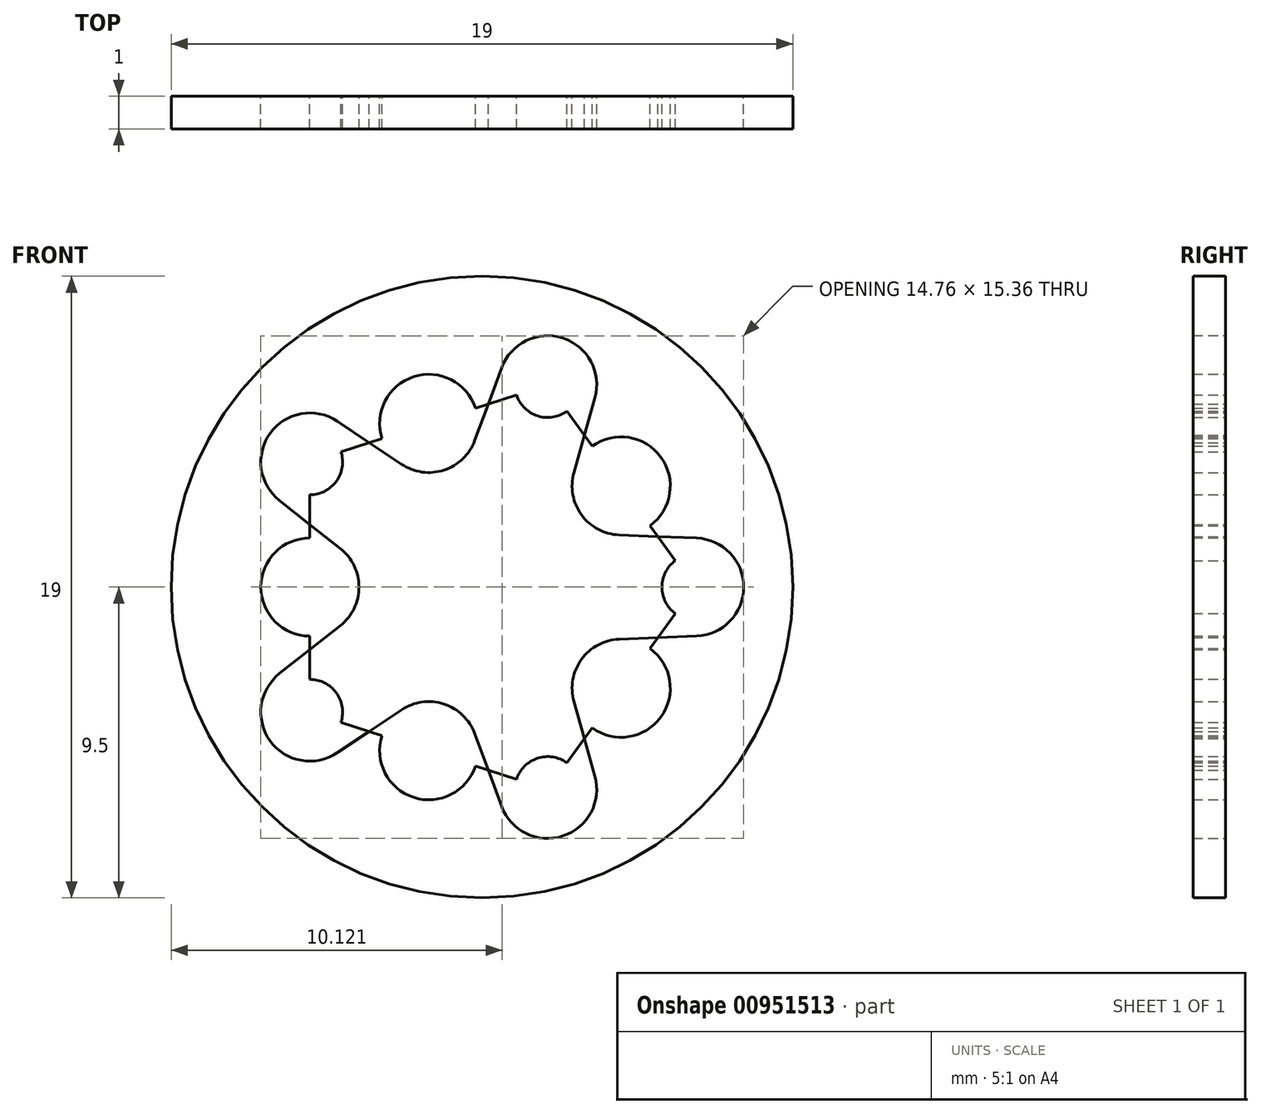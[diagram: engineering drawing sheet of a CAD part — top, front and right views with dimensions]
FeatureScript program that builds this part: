
annotation { "Feature Type Name" : "Feature", "Feature Type Description" : "" }
export const myFeature = defineFeature(function(context is Context, id is Id, definition is map)
    precondition{}
    {
        {
            var Q0;
            Q0=qCreatedBy(makeId("Front.planeOp"),FACE);
            var sketch = newSketch(context, id + "F0", { "sketchPlane" : qUnion([Q0])});
            skCircle(sketch, "E0", {"center": v(0, 0) * mm, "radius": 2.5 * mm});
            skCircle(sketch, "E1.cCircle", {"center": v(0, 0) * mm, "radius": 5.26 * mm, "construction": true});
            skLineSegment(sketch, "E1.0", {"start": v(-5.26, -3.82) * mm, "end": v(-5.26, 3.82) * mm});
            skLineSegment(sketch, "E1.1", {"start": v(-5.26, 3.82) * mm, "end": v(2, 6.18) * mm});
            skLineSegment(sketch, "E1.2", {"start": v(2, 6.18) * mm, "end": v(6.5, 0) * mm});
            skLineSegment(sketch, "E1.3", {"start": v(6.5, 0) * mm, "end": v(2, -6.18) * mm});
            skLineSegment(sketch, "E1.4", {"start": v(2, -6.18) * mm, "end": v(-5.26, -3.82) * mm});
            skPoint(sketch, "E1.0.midPoint", {"position": v(-5.26, 0) * mm});
            skCircle(sketch, "E2", {"center": v(-5.26, 3.82) * mm, "radius": 1 * mm});
            skCircle(sketch, "E3", {"center": v(2, 6.18) * mm, "radius": 1 * mm});
            skCircle(sketch, "E4", {"center": v(6.5, 0) * mm, "radius": 1 * mm});
            skCircle(sketch, "E5", {"center": v(2, -6.18) * mm, "radius": 1 * mm});
            skCircle(sketch, "E6", {"center": v(-5.26, -3.82) * mm, "radius": 1 * mm});
            skCircle(sketch, "E7", {"center": v(-5.26, 3.82) * mm, "radius": 1.5 * mm});
            skCircle(sketch, "E8", {"center": v(2, 6.18) * mm, "radius": 1.5 * mm});
            skCircle(sketch, "E9", {"center": v(6.5, 0) * mm, "radius": 1.5 * mm});
            skCircle(sketch, "E10", {"center": v(2, -6.18) * mm, "radius": 1.5 * mm});
            skCircle(sketch, "E11", {"center": v(-5.26, -3.82) * mm, "radius": 1.5 * mm});
            skCircle(sketch, "E12", {"center": v(-5.26, 0) * mm, "radius": 1.5 * mm});
            skCircle(sketch, "E13", {"center": v(-1.62, 5) * mm, "radius": 1.5 * mm});
            skCircle(sketch, "E14", {"center": v(4.25, 3.1) * mm, "radius": 1.5 * mm});
            skCircle(sketch, "E15", {"center": v(4.25, -3.1) * mm, "radius": 1.5 * mm});
            skCircle(sketch, "E16", {"center": v(-1.62, -5) * mm, "radius": 1.5 * mm});
            skLineSegment(sketch, "E17", {"start": v(-6.19, 2.64) * mm, "end": v(-4.33, 1.18) * mm});
            skLineSegment(sketch, "E18", {"start": v(-4.33, -1.18) * mm, "end": v(-6.19, -2.64) * mm});
            skLineSegment(sketch, "E19", {"start": v(-4.43, -5.07) * mm, "end": v(-2.46, -3.75) * mm});
            skLineSegment(sketch, "E20", {"start": v(-0.22, -4.48) * mm, "end": v(0.6, -6.7) * mm});
            skLineSegment(sketch, "E21", {"start": v(3.45, -5.77) * mm, "end": v(2.81, -3.5) * mm});
            skLineSegment(sketch, "E22", {"start": v(4.2, -1.6) * mm, "end": v(6.56, -1.5) * mm});
            skLineSegment(sketch, "E23", {"start": v(6.56, 1.5) * mm, "end": v(4.2, 1.6) * mm});
            skLineSegment(sketch, "E24", {"start": v(2.81, 3.5) * mm, "end": v(3.45, 5.77) * mm});
            skLineSegment(sketch, "E25", {"start": v(0.6, 6.7) * mm, "end": v(-0.22, 4.48) * mm});
            skLineSegment(sketch, "E26", {"start": v(-2.46, 3.75) * mm, "end": v(-4.43, 5.07) * mm});
            skLineSegment(sketch, "E27", {"start": v(1.5, 2) * mm, "end": v(1.5, -2) * mm});
            skCircle(sketch, "E28", {"center": v(0, 0) * mm, "radius": 9.5 * mm});
            skSolve(sketch);
        }
        {
            var Q0;
            {var subQ25=sQuery(id+"F0.wireOp",EDGE,"I007ogCC-rbbc-wW61-PL4D-8xOWQatjkpYn");var subQ26=sQuery(id+"F0.wireOp",EDGE,"E0");var subQ27=makeQuery(id+"F0.imprint","INTERSECT",VERTEX,{"disambiguationData":[OD(0.0)],"derivedFrom":[subQ26,subQ25]});Q0=makeQuery(id+"F0.imprint","IMPRINT",FACE,{"disambiguationData":[TD([[makeQuery(id+"F0.imprint","IMPRINT",EDGE,{"disambiguationData":[TD([[subQ27,1.0]])],"derivedFrom":subQ26}),-1.0]])]});}
            var Q1;
            {var subQ0=sQuery(id+"F0.wireOp",EDGE,"I007ogCC-rbbc-wW61-PL4D-8xOWQatjkpYn");Q1=makeQuery(id+"F0.imprint","IMPRINT",FACE,{"disambiguationData":[TD([[makeQuery(id+"F0.imprint","IMPRINT",EDGE,{"derivedFrom":subQ0}),1.0]])]});}
            var Q2;
            {var subQ0=sQuery(id+"F0.wireOp",EDGE,"E1.0");var subQ1=sQuery(id+"F0.wireOp",EDGE,"E2");var subQ2=makeQuery(id+"F0.imprint","INTERSECT",VERTEX,{"derivedFrom":[subQ1,subQ0]});Q2=makeQuery(id+"F0.imprint","IMPRINT",FACE,{"disambiguationData":[TD([[makeQuery(id+"F0.imprint","IMPRINT",EDGE,{"disambiguationData":[TD([[subQ2,-1.0]])],"derivedFrom":subQ1}),-1.0]])]});}
            var Q3;
            {var subQ0=sQuery(id+"F0.wireOp",EDGE,"E1.0");var subQ1=sQuery(id+"F0.wireOp",EDGE,"E2");var subQ2=makeQuery(id+"F0.imprint","INTERSECT",VERTEX,{"derivedFrom":[subQ1,subQ0]});Q3=makeQuery(id+"F0.imprint","IMPRINT",FACE,{"disambiguationData":[TD([[makeQuery(id+"F0.imprint","IMPRINT",EDGE,{"disambiguationData":[TD([[subQ2,1.0]])],"derivedFrom":subQ1}),-1.0]])]});}
            var Q4;
            {var subQ0=sQuery(id+"F0.wireOp",EDGE,"E1.1");var subQ1=sQuery(id+"F0.wireOp",EDGE,"E3");var subQ2=makeQuery(id+"F0.imprint","INTERSECT",VERTEX,{"derivedFrom":[subQ1,subQ0]});Q4=makeQuery(id+"F0.imprint","IMPRINT",FACE,{"disambiguationData":[TD([[makeQuery(id+"F0.imprint","IMPRINT",EDGE,{"disambiguationData":[TD([[subQ2,-1.0]])],"derivedFrom":subQ1}),-1.0]])]});}
            var Q5;
            {var subQ2=sQuery(id+"F0.wireOp",EDGE,"E1.1");var subQ4=sQuery(id+"F0.wireOp",EDGE,"E3");var subQ5=makeQuery(id+"F0.imprint","INTERSECT",VERTEX,{"derivedFrom":[subQ4,subQ2]});Q5=makeQuery(id+"F0.imprint","IMPRINT",FACE,{"disambiguationData":[TD([[makeQuery(id+"F0.imprint","IMPRINT",EDGE,{"disambiguationData":[TD([[subQ5,1.0]])],"derivedFrom":subQ4}),-1.0]])]});}
            var Q6;
            {var subQ0=sQuery(id+"F0.wireOp",EDGE,"E1.2");var subQ1=sQuery(id+"F0.wireOp",EDGE,"E4");var subQ2=makeQuery(id+"F0.imprint","INTERSECT",VERTEX,{"derivedFrom":[subQ1,subQ0]});Q6=makeQuery(id+"F0.imprint","IMPRINT",FACE,{"disambiguationData":[TD([[makeQuery(id+"F0.imprint","IMPRINT",EDGE,{"disambiguationData":[TD([[subQ2,-1.0]])],"derivedFrom":subQ1}),-1.0]])]});}
            var Q7;
            {var subQ2=sQuery(id+"F0.wireOp",EDGE,"E1.2");var subQ5=sQuery(id+"F0.wireOp",EDGE,"E4");var subQ8=makeQuery(id+"F0.imprint","INTERSECT",VERTEX,{"derivedFrom":[subQ5,subQ2]});Q7=makeQuery(id+"F0.imprint","IMPRINT",FACE,{"disambiguationData":[TD([[makeQuery(id+"F0.imprint","IMPRINT",EDGE,{"disambiguationData":[TD([[subQ8,1.0]])],"derivedFrom":subQ5}),-1.0]])]});}
            var Q8;
            {var subQ0=sQuery(id+"F0.wireOp",EDGE,"E1.3");var subQ1=sQuery(id+"F0.wireOp",EDGE,"E5");var subQ2=makeQuery(id+"F0.imprint","INTERSECT",VERTEX,{"derivedFrom":[subQ1,subQ0]});Q8=makeQuery(id+"F0.imprint","IMPRINT",FACE,{"disambiguationData":[TD([[makeQuery(id+"F0.imprint","IMPRINT",EDGE,{"disambiguationData":[TD([[subQ2,-1.0]])],"derivedFrom":subQ1}),-1.0]])]});}
            var Q9;
            {var subQ0=sQuery(id+"F0.wireOp",EDGE,"E1.3");var subQ1=sQuery(id+"F0.wireOp",EDGE,"E5");var subQ2=makeQuery(id+"F0.imprint","INTERSECT",VERTEX,{"derivedFrom":[subQ1,subQ0]});Q9=makeQuery(id+"F0.imprint","IMPRINT",FACE,{"disambiguationData":[TD([[makeQuery(id+"F0.imprint","IMPRINT",EDGE,{"disambiguationData":[TD([[subQ2,1.0]])],"derivedFrom":subQ1}),-1.0]])]});}
            var Q10;
            {var subQ0=sQuery(id+"F0.wireOp",EDGE,"E1.0");var subQ1=sQuery(id+"F0.wireOp",EDGE,"E6");var subQ2=makeQuery(id+"F0.imprint","INTERSECT",VERTEX,{"derivedFrom":[subQ1,subQ0]});Q10=makeQuery(id+"F0.imprint","IMPRINT",FACE,{"disambiguationData":[TD([[makeQuery(id+"F0.imprint","IMPRINT",EDGE,{"disambiguationData":[TD([[subQ2,1.0]])],"derivedFrom":subQ1}),-1.0]])]});}
            var Q11;
            {var subQ2=sQuery(id+"F0.wireOp",EDGE,"E1.0");var subQ4=sQuery(id+"F0.wireOp",EDGE,"E6");var subQ5=makeQuery(id+"F0.imprint","INTERSECT",VERTEX,{"derivedFrom":[subQ4,subQ2]});Q11=makeQuery(id+"F0.imprint","IMPRINT",FACE,{"disambiguationData":[TD([[makeQuery(id+"F0.imprint","IMPRINT",EDGE,{"disambiguationData":[TD([[subQ5,-1.0]])],"derivedFrom":subQ4}),-1.0]])]});}
            var Q12;
            {var subQ0=sQuery(id+"F0.wireOp",EDGE,"E18");var subQ1=sQuery(id+"F0.wireOp",EDGE,"E1.0");var subQ2=makeQuery(id+"F0.imprint","INTERSECT",VERTEX,{"derivedFrom":[subQ1,subQ0]});Q12=makeQuery(id+"F0.imprint","IMPRINT",FACE,{"disambiguationData":[TD([[makeQuery(id+"F0.imprint","IMPRINT",EDGE,{"disambiguationData":[TD([[subQ2,1.0]])],"derivedFrom":subQ1}),1.0]])]});}
            var Q13;
            {var subQ0=sQuery(id+"F0.wireOp",EDGE,"E17");var subQ1=sQuery(id+"F0.wireOp",EDGE,"E1.0");var subQ2=makeQuery(id+"F0.imprint","INTERSECT",VERTEX,{"derivedFrom":[subQ1,subQ0]});Q13=makeQuery(id+"F0.imprint","IMPRINT",FACE,{"disambiguationData":[TD([[makeQuery(id+"F0.imprint","IMPRINT",EDGE,{"disambiguationData":[TD([[subQ2,-1.0]])],"derivedFrom":subQ1}),1.0]])]});}
            var Q14;
            {var subQ0=sQuery(id+"F0.wireOp",EDGE,"E26");var subQ1=sQuery(id+"F0.wireOp",EDGE,"E1.1");var subQ2=makeQuery(id+"F0.imprint","INTERSECT",VERTEX,{"derivedFrom":[subQ1,subQ0]});Q14=makeQuery(id+"F0.imprint","IMPRINT",FACE,{"disambiguationData":[TD([[makeQuery(id+"F0.imprint","IMPRINT",EDGE,{"disambiguationData":[TD([[subQ2,1.0]])],"derivedFrom":subQ1}),1.0]])]});}
            var Q15;
            {var subQ0=sQuery(id+"F0.wireOp",EDGE,"E25");var subQ1=sQuery(id+"F0.wireOp",EDGE,"E1.1");var subQ2=makeQuery(id+"F0.imprint","INTERSECT",VERTEX,{"derivedFrom":[subQ1,subQ0]});Q15=makeQuery(id+"F0.imprint","IMPRINT",FACE,{"disambiguationData":[TD([[makeQuery(id+"F0.imprint","IMPRINT",EDGE,{"disambiguationData":[TD([[subQ2,-1.0]])],"derivedFrom":subQ1}),1.0]])]});}
            var Q16;
            {var subQ0=sQuery(id+"F0.wireOp",EDGE,"E23");var subQ1=sQuery(id+"F0.wireOp",EDGE,"E1.2");var subQ2=makeQuery(id+"F0.imprint","INTERSECT",VERTEX,{"derivedFrom":[subQ1,subQ0]});Q16=makeQuery(id+"F0.imprint","IMPRINT",FACE,{"disambiguationData":[TD([[makeQuery(id+"F0.imprint","IMPRINT",EDGE,{"disambiguationData":[TD([[subQ2,-1.0]])],"derivedFrom":subQ1}),1.0]])]});}
            var Q17;
            {var subQ0=sQuery(id+"F0.wireOp",EDGE,"E22");var subQ1=sQuery(id+"F0.wireOp",EDGE,"E1.3");var subQ2=makeQuery(id+"F0.imprint","INTERSECT",VERTEX,{"derivedFrom":[subQ1,subQ0]});Q17=makeQuery(id+"F0.imprint","IMPRINT",FACE,{"disambiguationData":[TD([[makeQuery(id+"F0.imprint","IMPRINT",EDGE,{"disambiguationData":[TD([[subQ2,1.0]])],"derivedFrom":subQ1}),1.0]])]});}
            var Q18;
            {var subQ0=sQuery(id+"F0.wireOp",EDGE,"E21");var subQ1=sQuery(id+"F0.wireOp",EDGE,"E1.3");var subQ2=makeQuery(id+"F0.imprint","INTERSECT",VERTEX,{"derivedFrom":[subQ1,subQ0]});Q18=makeQuery(id+"F0.imprint","IMPRINT",FACE,{"disambiguationData":[TD([[makeQuery(id+"F0.imprint","IMPRINT",EDGE,{"disambiguationData":[TD([[subQ2,-1.0]])],"derivedFrom":subQ1}),1.0]])]});}
            var Q19;
            {var subQ0=sQuery(id+"F0.wireOp",EDGE,"E20");var subQ1=sQuery(id+"F0.wireOp",EDGE,"E1.4");var subQ2=makeQuery(id+"F0.imprint","INTERSECT",VERTEX,{"derivedFrom":[subQ1,subQ0]});Q19=makeQuery(id+"F0.imprint","IMPRINT",FACE,{"disambiguationData":[TD([[makeQuery(id+"F0.imprint","IMPRINT",EDGE,{"disambiguationData":[TD([[subQ2,1.0]])],"derivedFrom":subQ1}),1.0]])]});}
            var Q20;
            {var subQ0=sQuery(id+"F0.wireOp",EDGE,"E19");var subQ1=sQuery(id+"F0.wireOp",EDGE,"E1.4");var subQ2=makeQuery(id+"F0.imprint","INTERSECT",VERTEX,{"derivedFrom":[subQ1,subQ0]});Q20=makeQuery(id+"F0.imprint","IMPRINT",FACE,{"disambiguationData":[TD([[makeQuery(id+"F0.imprint","IMPRINT",EDGE,{"disambiguationData":[TD([[subQ2,-1.0]])],"derivedFrom":subQ1}),1.0]])]});}
            var Q21;
            {var subQ0=sQuery(id+"F0.wireOp",EDGE,"E24");var subQ1=sQuery(id+"F0.wireOp",EDGE,"E1.2");var subQ2=makeQuery(id+"F0.imprint","INTERSECT",VERTEX,{"derivedFrom":[subQ1,subQ0]});Q21=makeQuery(id+"F0.imprint","IMPRINT",FACE,{"disambiguationData":[TD([[makeQuery(id+"F0.imprint","IMPRINT",EDGE,{"disambiguationData":[TD([[subQ2,1.0]])],"derivedFrom":subQ1}),1.0]])]});}
            var Q22;
            {var subQ0=sQuery(id+"F0.wireOp",EDGE,"E27");Q22=makeQuery(id+"F0.imprint","IMPRINT",FACE,{"disambiguationData":[TD([[makeQuery(id+"F0.imprint","IMPRINT",EDGE,{"derivedFrom":subQ0}),1.0]])]});}
            var Q23;
            {var subQ0=sQuery(id+"F0.wireOp",EDGE,"E27");Q23=makeQuery(id+"F0.imprint","IMPRINT",FACE,{"disambiguationData":[TD([[makeQuery(id+"F0.imprint","IMPRINT",EDGE,{"derivedFrom":subQ0}),-1.0]])]});}
            var Q24;
            Q24=makeQuery(id+"F0.imprint","IMPRINT",FACE,{"disambiguationData":[TD([[makeQuery(id+"F0.imprint","IMPRINT",EDGE,{"derivedFrom":sQuery(id+"F0.wireOp",EDGE,"E28")}),1.0]])]});
            var Q25;
            {var subQ0=sQuery(id+"F0.wireOp",EDGE,"E14");var subQ1=sQuery(id+"F0.wireOp",EDGE,"E1.2");var subQ2=makeQuery(id+"F0.imprint","INTERSECT",VERTEX,{"disambiguationData":[OD(1.0)],"derivedFrom":[subQ1,subQ0]});Q25=makeQuery(id+"F0.imprint","IMPRINT",FACE,{"disambiguationData":[TD([[makeQuery(id+"F0.imprint","IMPRINT",EDGE,{"disambiguationData":[TD([[subQ2,-1.0]])],"derivedFrom":subQ1}),-1.0]])]});}
            var Q26;
            {var subQ0=sQuery(id+"F0.wireOp",EDGE,"E24");var subQ1=sQuery(id+"F0.wireOp",EDGE,"E1.2");var subQ2=makeQuery(id+"F0.imprint","INTERSECT",VERTEX,{"derivedFrom":[subQ1,subQ0]});Q26=makeQuery(id+"F0.imprint","IMPRINT",FACE,{"disambiguationData":[TD([[makeQuery(id+"F0.imprint","IMPRINT",EDGE,{"disambiguationData":[TD([[subQ2,-1.0]])],"derivedFrom":subQ1}),-1.0]])]});}
            var Q27;
            {var subQ0=sQuery(id+"F0.wireOp",EDGE,"E13");var subQ1=sQuery(id+"F0.wireOp",EDGE,"E1.1");var subQ2=makeQuery(id+"F0.imprint","INTERSECT",VERTEX,{"disambiguationData":[OD(1.0)],"derivedFrom":[subQ1,subQ0]});Q27=makeQuery(id+"F0.imprint","IMPRINT",FACE,{"disambiguationData":[TD([[makeQuery(id+"F0.imprint","IMPRINT",EDGE,{"disambiguationData":[TD([[subQ2,-1.0]])],"derivedFrom":subQ1}),-1.0]])]});}
            var Q28;
            {var subQ0=sQuery(id+"F0.wireOp",EDGE,"E26");var subQ1=sQuery(id+"F0.wireOp",EDGE,"E1.1");var subQ2=makeQuery(id+"F0.imprint","INTERSECT",VERTEX,{"derivedFrom":[subQ1,subQ0]});Q28=makeQuery(id+"F0.imprint","IMPRINT",FACE,{"disambiguationData":[TD([[makeQuery(id+"F0.imprint","IMPRINT",EDGE,{"disambiguationData":[TD([[subQ2,-1.0]])],"derivedFrom":subQ1}),-1.0]])]});}
            var Q29;
            {var subQ0=sQuery(id+"F0.wireOp",EDGE,"E12");var subQ1=sQuery(id+"F0.wireOp",EDGE,"E1.0");var subQ2=makeQuery(id+"F0.imprint","INTERSECT",VERTEX,{"disambiguationData":[OD(1.0)],"derivedFrom":[subQ1,subQ0]});Q29=makeQuery(id+"F0.imprint","IMPRINT",FACE,{"disambiguationData":[TD([[makeQuery(id+"F0.imprint","IMPRINT",EDGE,{"disambiguationData":[TD([[subQ2,-1.0]])],"derivedFrom":subQ1}),-1.0]])]});}
            var Q30;
            {var subQ0=sQuery(id+"F0.wireOp",EDGE,"E16");var subQ1=sQuery(id+"F0.wireOp",EDGE,"E1.4");var subQ2=makeQuery(id+"F0.imprint","INTERSECT",VERTEX,{"disambiguationData":[OD(1.0)],"derivedFrom":[subQ1,subQ0]});Q30=makeQuery(id+"F0.imprint","IMPRINT",FACE,{"disambiguationData":[TD([[makeQuery(id+"F0.imprint","IMPRINT",EDGE,{"disambiguationData":[TD([[subQ2,-1.0]])],"derivedFrom":subQ1}),-1.0]])]});}
            var Q31;
            {var subQ0=sQuery(id+"F0.wireOp",EDGE,"E20");var subQ1=sQuery(id+"F0.wireOp",EDGE,"E1.4");var subQ2=makeQuery(id+"F0.imprint","INTERSECT",VERTEX,{"derivedFrom":[subQ1,subQ0]});Q31=makeQuery(id+"F0.imprint","IMPRINT",FACE,{"disambiguationData":[TD([[makeQuery(id+"F0.imprint","IMPRINT",EDGE,{"disambiguationData":[TD([[subQ2,-1.0]])],"derivedFrom":subQ1}),-1.0]])]});}
            var Q32;
            {var subQ0=sQuery(id+"F0.wireOp",EDGE,"E15");var subQ1=sQuery(id+"F0.wireOp",EDGE,"E1.3");var subQ2=makeQuery(id+"F0.imprint","INTERSECT",VERTEX,{"disambiguationData":[OD(1.0)],"derivedFrom":[subQ1,subQ0]});Q32=makeQuery(id+"F0.imprint","IMPRINT",FACE,{"disambiguationData":[TD([[makeQuery(id+"F0.imprint","IMPRINT",EDGE,{"disambiguationData":[TD([[subQ2,-1.0]])],"derivedFrom":subQ1}),-1.0]])]});}
            var Q33;
            {var subQ0=sQuery(id+"F0.wireOp",EDGE,"E22");var subQ1=sQuery(id+"F0.wireOp",EDGE,"E1.3");var subQ2=makeQuery(id+"F0.imprint","INTERSECT",VERTEX,{"derivedFrom":[subQ1,subQ0]});Q33=makeQuery(id+"F0.imprint","IMPRINT",FACE,{"disambiguationData":[TD([[makeQuery(id+"F0.imprint","IMPRINT",EDGE,{"disambiguationData":[TD([[subQ2,-1.0]])],"derivedFrom":subQ1}),-1.0]])]});}
            var Q34;
            {var subQ0=sQuery(id+"F0.wireOp",EDGE,"E18");var subQ1=sQuery(id+"F0.wireOp",EDGE,"E1.0");var subQ2=makeQuery(id+"F0.imprint","INTERSECT",VERTEX,{"derivedFrom":[subQ1,subQ0]});Q34=makeQuery(id+"F0.imprint","IMPRINT",FACE,{"disambiguationData":[TD([[makeQuery(id+"F0.imprint","IMPRINT",EDGE,{"disambiguationData":[TD([[subQ2,-1.0]])],"derivedFrom":subQ1}),-1.0]])]});}
            extrude(context, id + "F1", {"entities" : qUnion([Q0, Q1, Q2, Q3, Q4, Q5, Q6, Q7, Q8, Q9, Q10, Q11, Q12, Q13, Q14, Q15, Q16, Q17, Q18, Q19, Q20, Q21, Q22, Q23, Q24, Q25, Q26, Q27, Q28, Q29, Q30, Q31, Q32, Q33, Q34]), "depth" : 1 * mm, "offsetDistance" : 25 * mm});
        }
    });
